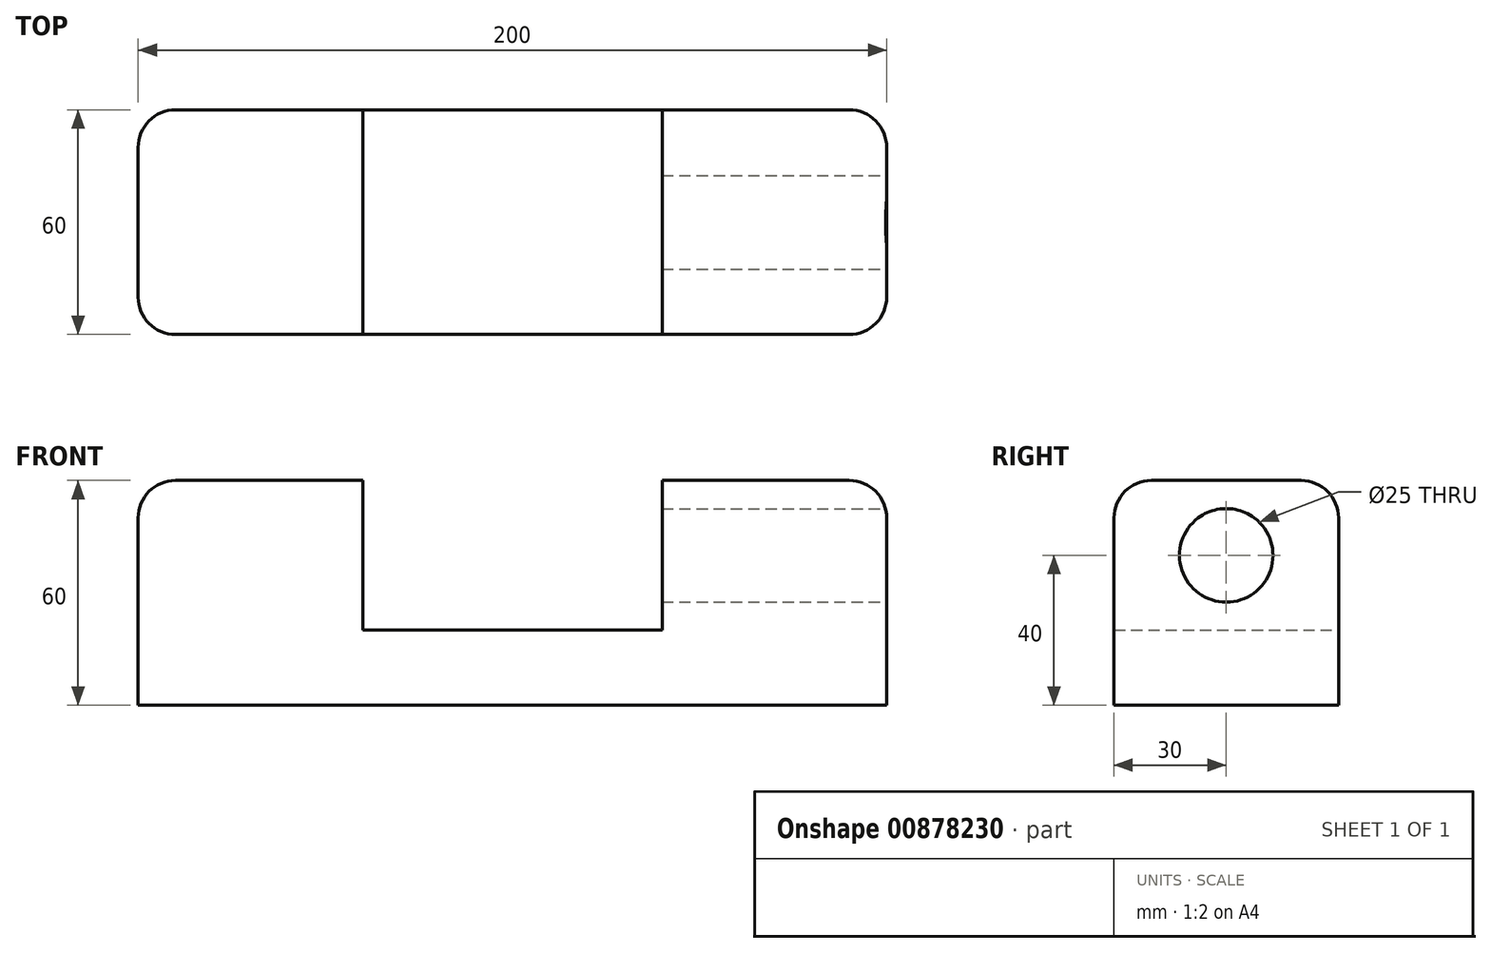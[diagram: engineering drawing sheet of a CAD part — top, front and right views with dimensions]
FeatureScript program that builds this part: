
annotation { "Feature Type Name" : "Feature", "Feature Type Description" : "" }
export const myFeature = defineFeature(function(context is Context, id is Id, definition is map)
    precondition{}
    {
        {
            var Q0;
            Q0=qCreatedBy(makeId("Front.planeOp"),FACE);
            var sketch = newSketch(context, id + "F0", { "sketchPlane" : qUnion([Q0])});
            skLineSegment(sketch, "E0.bottom", {"start": v(0, 0) * mm, "end": v(200, 0) * mm});
            skLineSegment(sketch, "E0.left", {"start": v(0, 0) * mm, "end": v(0, 60) * mm});
            skLineSegment(sketch, "E0.right", {"start": v(200, 0) * mm, "end": v(200, 60) * mm});
            skLineSegment(sketch, "E1", {"start": v(0, 60) * mm, "end": v(60, 60) * mm});
            skLineSegment(sketch, "E2", {"start": v(60, 60) * mm, "end": v(60, 20) * mm});
            skLineSegment(sketch, "E3", {"start": v(60, 20) * mm, "end": v(140, 20) * mm});
            skLineSegment(sketch, "E4", {"start": v(140, 20) * mm, "end": v(140, 60) * mm});
            skLineSegment(sketch, "E5", {"start": v(140, 60) * mm, "end": v(200, 60) * mm});
            skSolve(sketch);
        }
        {
            var Q0;
            Q0=makeQuery(id+"F0.imprint","IMPRINT",FACE,{"disambiguationData":[TD([[makeQuery(id+"F0.imprint","IMPRINT",EDGE,{"derivedFrom":sQuery(id+"F0.wireOp",EDGE,"E0.bottom")}),1.0]])]});
            extrude(context, id + "F1", {"entities" : qUnion([Q0]), "depth" : 60 * mm, "offsetDistance" : 25 * mm});
        }
        {
            var Q0;
            Q0=makeQuery(id+"F1.opExtrude","SWEPT_FACE",FACE,{"disambiguationData":[OSD([sQuery(id+"F0.wireOp",EDGE,"E0.right")])]});
            var sketch = newSketch(context, id + "F2", { "sketchPlane" : qUnion([Q0])});
            skCircle(sketch, "E6", {"center": v(-30, 40) * mm, "radius": 12.5 * mm});
            skSolve(sketch);
        }
        {
            var Q0;
            Q0=makeQuery(id+"F2.imprint","IMPRINT",FACE,{"disambiguationData":[TD([[makeQuery(id+"F2.imprint","IMPRINT",EDGE,{"derivedFrom":sQuery(id+"F2.wireOp",EDGE,"E6")}),1.0]])]});
            extrude(context, id + "F3", {"entities" : qUnion([Q0]), "operationType" : NewBodyOperationType.REMOVE, "oppositeDirection" : true, "depth" : 70 * mm, "offsetDistance" : 25 * mm});
        }
        {
            var Q0;
            Q0=makeQuery(id+"F1.opExtrude","CAP_EDGE",EDGE,{"disambiguationData":[OSD([sQuery(id+"F0.wireOp",EDGE,"E0.left")])],"isStart":false});
            var Q1;
            Q1=makeQuery(id+"F1.opExtrude","SWEPT_EDGE",EDGE,{"disambiguationData":[OSD([sQuery(id+"F0.wireOp",EDGE,"E0.left"),sQuery(id+"F0.wireOp",EDGE,"E1")])]});
            var Q2;
            Q2=makeQuery(id+"F1.opExtrude","CAP_EDGE",EDGE,{"disambiguationData":[OSD([sQuery(id+"F0.wireOp",EDGE,"E1")])],"isStart":true});
            var Q3;
            Q3=makeQuery(id+"F1.opExtrude","CAP_EDGE",EDGE,{"disambiguationData":[OSD([sQuery(id+"F0.wireOp",EDGE,"E1")])],"isStart":false});
            var Q4;
            Q4=makeQuery(id+"F1.opExtrude","CAP_EDGE",EDGE,{"disambiguationData":[OSD([sQuery(id+"F0.wireOp",EDGE,"E0.left")])],"isStart":true});
            var Q5;
            Q5=makeQuery(id+"F1.opExtrude","CAP_EDGE",EDGE,{"disambiguationData":[OSD([sQuery(id+"F0.wireOp",EDGE,"E5")])],"isStart":false});
            var Q6;
            Q6=makeQuery(id+"F1.opExtrude","CAP_EDGE",EDGE,{"disambiguationData":[OSD([sQuery(id+"F0.wireOp",EDGE,"E5")])],"isStart":true});
            var Q7;
            Q7=makeQuery(id+"F1.opExtrude","SWEPT_EDGE",EDGE,{"disambiguationData":[OSD([sQuery(id+"F0.wireOp",EDGE,"E0.right"),sQuery(id+"F0.wireOp",EDGE,"E5")])]});
            var Q8;
            Q8=makeQuery(id+"F1.opExtrude","CAP_EDGE",EDGE,{"disambiguationData":[OSD([sQuery(id+"F0.wireOp",EDGE,"E0.right")])],"isStart":false});
            var Q9;
            Q9=makeQuery(id+"F1.opExtrude","CAP_EDGE",EDGE,{"disambiguationData":[OSD([sQuery(id+"F0.wireOp",EDGE,"E0.right")])],"isStart":true});
            fillet(context, id + "F4", {"entities" : qUnion([Q0, Q1, Q2, Q3, Q4, Q5, Q6, Q7, Q8, Q9]), "radius" : 10 * mm, "tangentPropagation" : true, "allowEdgeOverflow" : false});
        }
    });
